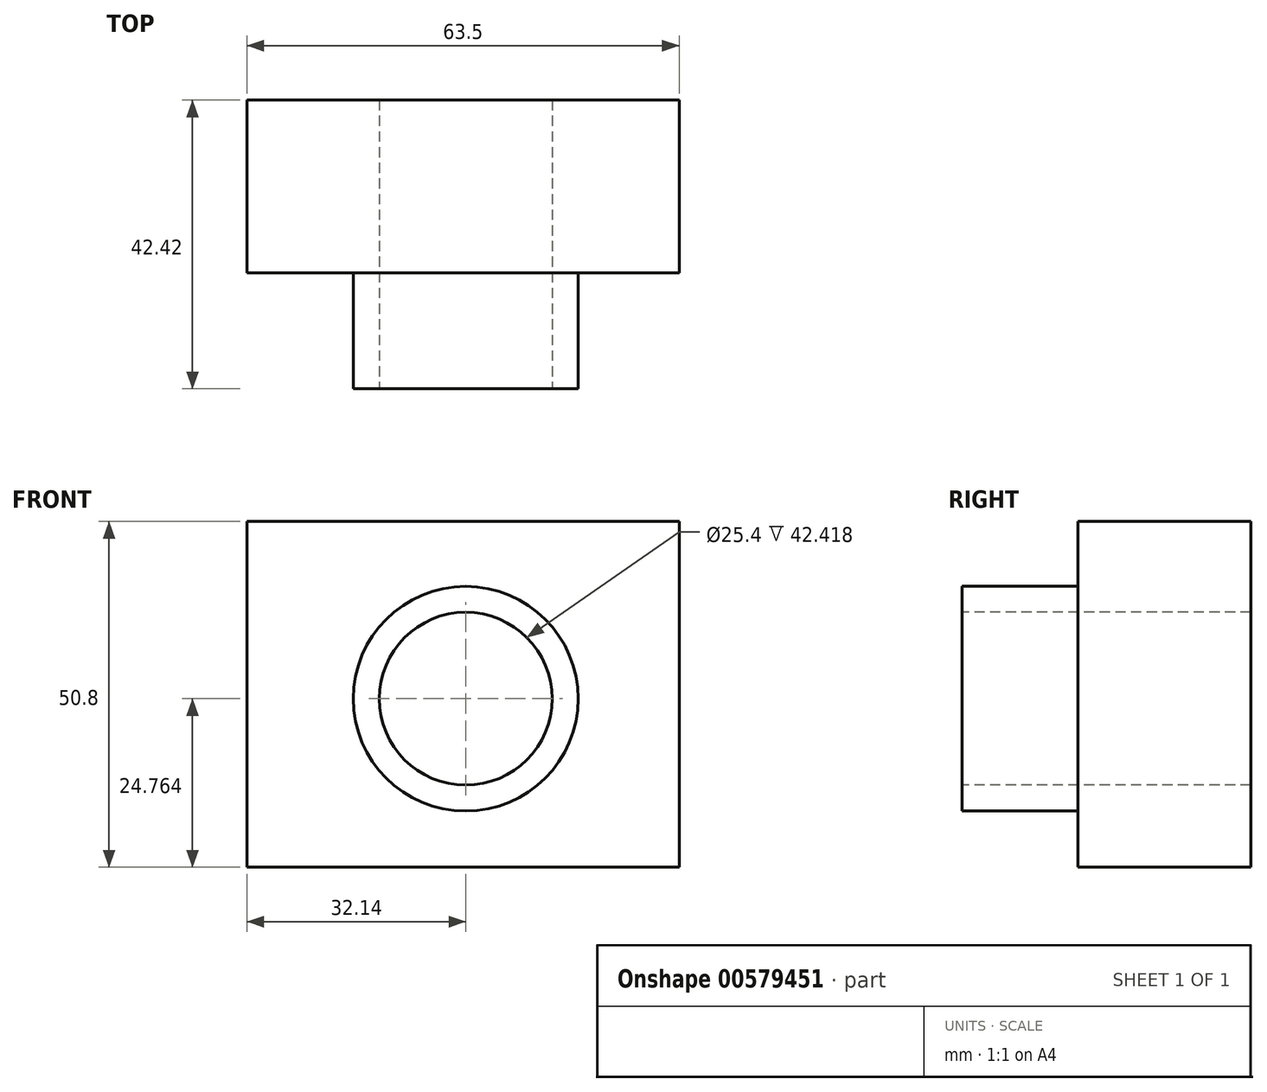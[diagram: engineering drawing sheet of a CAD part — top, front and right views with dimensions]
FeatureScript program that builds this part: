
annotation { "Feature Type Name" : "Feature", "Feature Type Description" : "" }
export const myFeature = defineFeature(function(context is Context, id is Id, definition is map)
    precondition{}
    {
        {
            var Q0;
            Q0=qCreatedBy(makeId("Front.planeOp"),FACE);
            var sketch = newSketch(context, id + "F0", { "sketchPlane" : qUnion([Q0])});
            skLineSegment(sketch, "E0.bottom", {"start": v(-32.14, 19.73) * mm, "end": v(31.36, 19.73) * mm});
            skLineSegment(sketch, "E0.top", {"start": v(-32.14, -31.07) * mm, "end": v(31.36, -31.07) * mm});
            skLineSegment(sketch, "E0.left", {"start": v(-32.14, 19.73) * mm, "end": v(-32.14, -31.07) * mm});
            skLineSegment(sketch, "E0.right", {"start": v(31.36, 19.73) * mm, "end": v(31.36, -31.07) * mm});
            skSolve(sketch);
        }
        {
            var Q0;
            Q0=makeQuery(id+"F0.imprint","IMPRINT",FACE,{"disambiguationData":[TD([[makeQuery(id+"F0.imprint","IMPRINT",EDGE,{"derivedFrom":sQuery(id+"F0.wireOp",EDGE,"E0.bottom")}),-1.0]])]});
            extrude(context, id + "F1", {"entities" : qUnion([Q0]), "depth" : 25.4 * mm, "offsetDistance" : 25.4 * mm});
        }
        {
            var Q0;
            Q0=makeQuery(id+"F1.opExtrude","CAP_FACE",FACE,{"disambiguationData":[OSD([sQuery(id+"F0.wireOp",EDGE,"E0.bottom"),sQuery(id+"F0.wireOp",EDGE,"E0.top"),sQuery(id+"F0.wireOp",EDGE,"E0.left"),sQuery(id+"F0.wireOp",EDGE,"E0.right")])],"isStart":false});
            var sketch = newSketch(context, id + "F2", { "sketchPlane" : qUnion([Q0])});
            skCircle(sketch, "E1", {"center": v(0, -6.3) * mm, "radius": 12.7 * mm});
            skSolve(sketch);
        }
        {
            var Q0;
            Q0=makeQuery(id+"F2.imprint","IMPRINT",FACE,{"disambiguationData":[TD([[makeQuery(id+"F2.imprint","IMPRINT",EDGE,{"derivedFrom":sQuery(id+"F2.wireOp",EDGE,"E1")}),1.0]])]});
            extrude(context, id + "F3", {"entities" : qUnion([Q0]), "operationType" : NewBodyOperationType.REMOVE, "endBound" : BoundingType.THROUGH_ALL, "oppositeDirection" : true, "depth" : 25.4 * mm, "offsetDistance" : 25.4 * mm});
        }
        {
            var Q0;
            Q0=makeQuery(id+"F1.opExtrude","CAP_FACE",FACE,{"disambiguationData":[OSD([sQuery(id+"F0.wireOp",EDGE,"E0.bottom"),sQuery(id+"F0.wireOp",EDGE,"E0.top"),sQuery(id+"F0.wireOp",EDGE,"E0.left"),sQuery(id+"F0.wireOp",EDGE,"E0.right")])],"isStart":false});
            var sketch = newSketch(context, id + "F4", { "sketchPlane" : qUnion([Q0])});
            skCircle(sketch, "E2", {"center": v(0, -6.3) * mm, "radius": 16.51 * mm});
            skSolve(sketch);
        }
        {
            var Q0;
            Q0=makeQuery(id+"F4.imprint","IMPRINT",FACE,{"disambiguationData":[TD([[makeQuery(id+"F4.imprint","IMPRINT",EDGE,{"derivedFrom":sQuery(id+"F4.wireOp",EDGE,"E2")}),1.0]])]});
            extrude(context, id + "F5", {"entities" : qUnion([Q0]), "operationType" : NewBodyOperationType.ADD, "depth" : 17.02 * mm, "offsetDistance" : 25.4 * mm});
        }
    });
